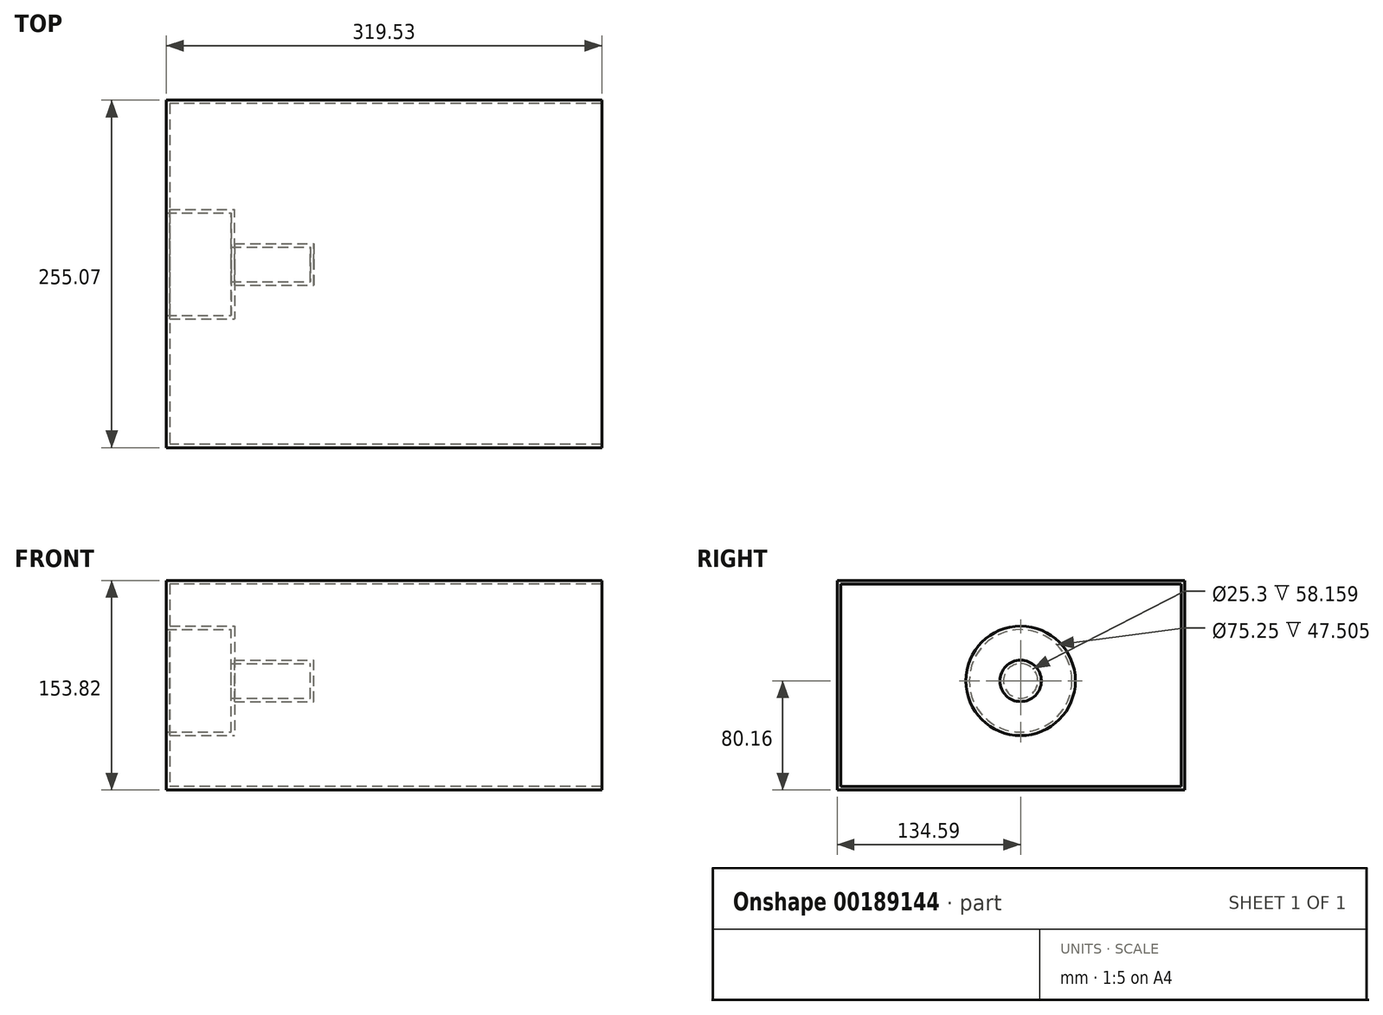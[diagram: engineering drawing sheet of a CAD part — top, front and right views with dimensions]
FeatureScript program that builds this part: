
annotation { "Feature Type Name" : "Feature", "Feature Type Description" : "" }
export const myFeature = defineFeature(function(context is Context, id is Id, definition is map)
    precondition{}
    {
        {
            var Q0;
            Q0=qCreatedBy(makeId("Top.planeOp"),FACE);
            var sketch = newSketch(context, id + "F0", { "sketchPlane" : qUnion([Q0])});
            skLineSegment(sketch, "E0.bottom", {"start": v(-58.16, 37.62) * mm, "end": v(60.79, 37.62) * mm});
            skLineSegment(sketch, "E0.top", {"start": v(-58.16, 12.65) * mm, "end": v(60.79, 12.65) * mm});
            skLineSegment(sketch, "E0.left", {"start": v(-58.16, 37.62) * mm, "end": v(-58.16, 12.65) * mm});
            skLineSegment(sketch, "E0.right", {"start": v(60.79, 37.62) * mm, "end": v(60.79, 12.65) * mm});
            skLineSegment(sketch, "E1", {"start": v(76.81, 0) * mm, "end": v(-62.8, 0) * mm});
            skSolve(sketch);
        }
        {
            var Q0;
            Q0=makeQuery(id+"F0.imprint","IMPRINT",FACE,{"disambiguationData":[TD([[makeQuery(id+"F0.imprint","IMPRINT",EDGE,{"derivedFrom":sQuery(id+"F0.wireOp",EDGE,"E0.bottom")}),-1.0]])]});
            var Q1;
            Q1=sQuery(id+"F0.wireOp",EDGE,"E1");
            revolve(context, id + "F1", {"entities" : qUnion([Q0]), "axis" : qUnion([Q1]), "revolveType" : RevolveType.FULL});
        }
        {
            var Q0;
            Q0=qCreatedBy(makeId("Right.planeOp"),FACE);
            var sketch = newSketch(context, id + "F2", { "sketchPlane" : qUnion([Q0])});
            skLineSegment(sketch, "E2.bottom", {"start": v(120.48, 73.66) * mm, "end": v(-134.59, 73.66) * mm});
            skLineSegment(sketch, "E2.top", {"start": v(120.48, -80.16) * mm, "end": v(-134.59, -80.16) * mm});
            skLineSegment(sketch, "E2.left", {"start": v(120.48, 73.66) * mm, "end": v(120.48, -80.16) * mm});
            skLineSegment(sketch, "E2.right", {"start": v(-134.59, 73.66) * mm, "end": v(-134.59, -80.16) * mm});
            skSolve(sketch);
        }
        {
            var Q0;
            Q0=makeQuery(id+"F2.imprint","IMPRINT",FACE,{"disambiguationData":[TD([[makeQuery(id+"F2.imprint","IMPRINT",EDGE,{"derivedFrom":sQuery(id+"F2.wireOp",EDGE,"E2.bottom")}),1.0]])]});
            extrude(context, id + "F3", {"entities" : qUnion([Q0]), "operationType" : NewBodyOperationType.ADD, "depth" : 213.87 * mm});
        }
        {
            var Q0;
            {var subQ0=sQuery(id+"F2.wireOp",EDGE,"E2.left");var subQ1=sQuery(id+"F2.wireOp",EDGE,"E2.top");var subQ2=sQuery(id+"F2.wireOp",EDGE,"E2.bottom");var subQ3=sQuery(id+"F2.wireOp",EDGE,"E2.right");Q0=makeQuery(id+"F3.boolean.opBoolean","SPLIT",FACE,{"disambiguationData":[TD([makeQuery(id+"F1.opRevolve","SWEPT_FACE",FACE,{"disambiguationData":[OSD([sQuery(id+"F0.wireOp",EDGE,"E0.bottom")])]})])],"derivedFrom":makeQuery(id+"F3.opExtrude","CAP_FACE",FACE,{"disambiguationData":[OSD([subQ2,subQ1,subQ0,subQ3])],"isStart":true})});}
            extrude(context, id + "F4", {"entities" : qUnion([Q0]), "operationType" : NewBodyOperationType.ADD, "depth" : 105.66 * mm});
        }
        {
            var Q0;
            Q0=makeQuery(id+"F3.opExtrude","CAP_FACE",FACE,{"disambiguationData":[OSD([sQuery(id+"F2.wireOp",EDGE,"E2.bottom"),sQuery(id+"F2.wireOp",EDGE,"E2.top"),sQuery(id+"F2.wireOp",EDGE,"E2.left"),sQuery(id+"F2.wireOp",EDGE,"E2.right")])],"isStart":false});
            shell(context, id + "F5", {"entities" : qUnion([Q0]), "thickness" : 2.54 * mm});
        }
    });
